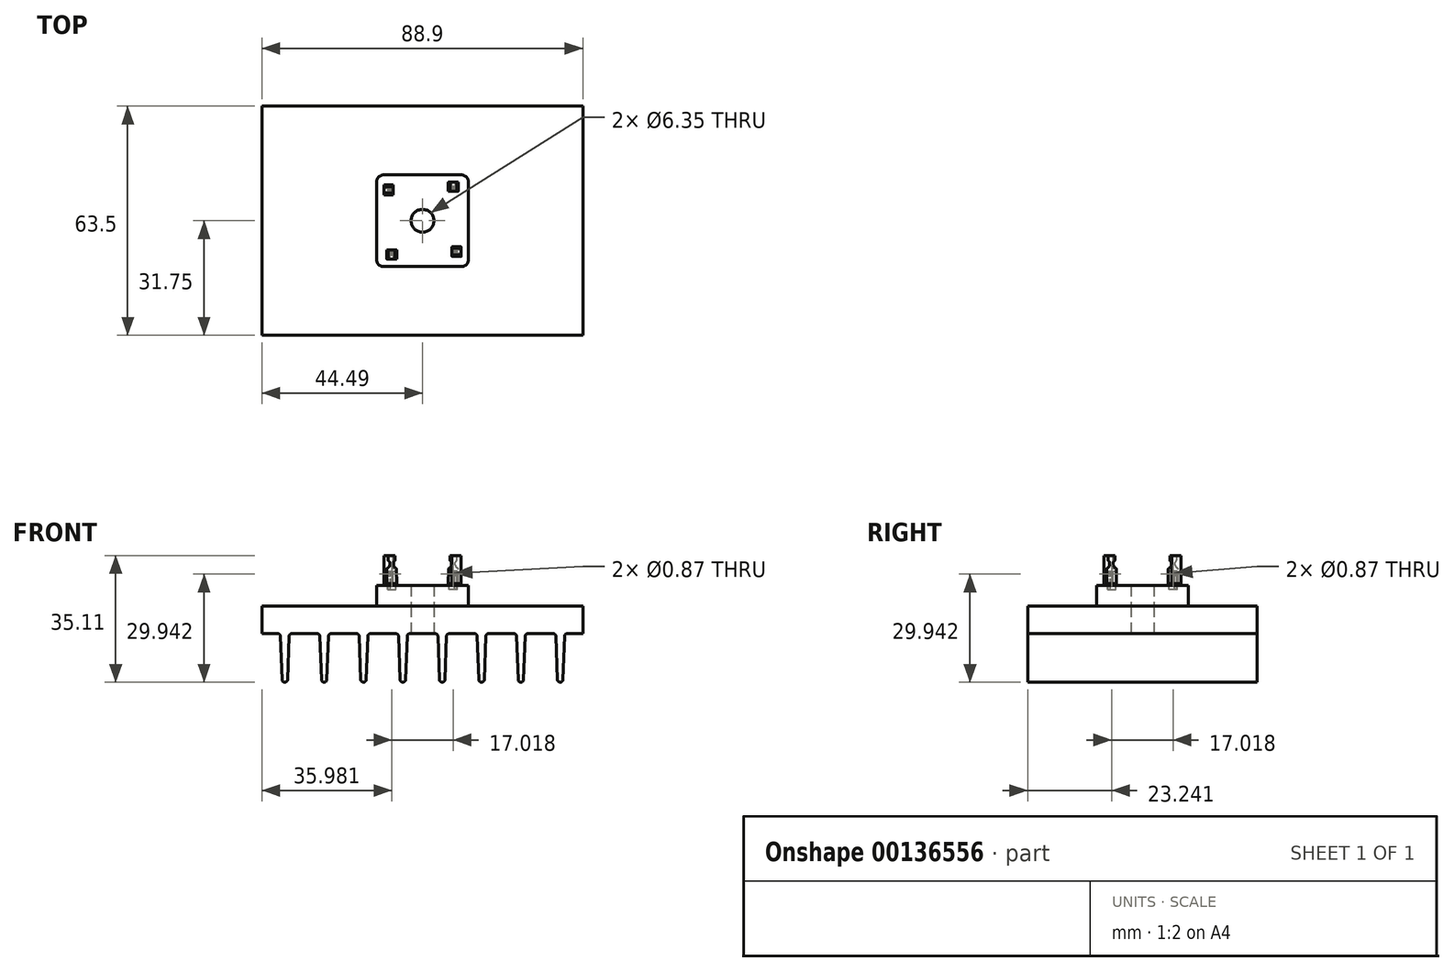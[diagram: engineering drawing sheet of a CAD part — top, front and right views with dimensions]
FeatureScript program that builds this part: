
annotation { "Feature Type Name" : "Feature", "Feature Type Description" : "" }
export const myFeature = defineFeature(function(context is Context, id is Id, definition is map)
    precondition{}
    {
        {
            var Q0;
            Q0=qCreatedBy(makeId("Front.planeOp"),FACE);
            var sketch = newSketch(context, id + "F0", { "sketchPlane" : qUnion([Q0])});
            skLineSegment(sketch, "E0.bottom", {"start": v(-44.49, 7.62) * mm, "end": v(44.41, 7.62) * mm});
            skLineSegment(sketch, "E0.top", {"start": v(-44.49, 0) * mm, "end": v(-40.1, 0) * mm});
            skLineSegment(sketch, "E0.left", {"start": v(-44.49, 7.62) * mm, "end": v(-44.49, 0) * mm});
            skLineSegment(sketch, "E0.right", {"start": v(44.41, 7.62) * mm, "end": v(44.41, 0) * mm});
            skPoint(sketch, "E1", {"position": v(0, 0) * mm});
            skArc(sketch, "E2", {"start": v(-38.9, -12.73) * mm, "mid": v(-38.14, -13.46) * mm, "end": v(-37.38, -12.73) * mm});
            skLineSegment(sketch, "E3", {"start": v(-37.38, -12.73) * mm, "end": v(-36.95, -0.73) * mm});
            skLineSegment(sketch, "E4", {"start": v(-36.92, 0) * mm, "end": v(-39.36, 0) * mm});
            skLineSegment(sketch, "E5", {"start": v(-39.33, -0.73) * mm, "end": v(-38.9, -12.73) * mm});
            skLineSegment(sketch, "E6", {"start": v(-38.14, -12.7) * mm, "end": v(-38.14, 0) * mm, "construction": true});
            skPoint(sketch, "E7.newPointB", {"position": v(44.49, 0) * mm});
            skArc(sketch, "E7.filletArc", {"start": v(-39.33, -0.73) * mm, "mid": v(-39.56, -0.21) * mm, "end": v(-40.1, 0) * mm});
            skLineSegment(sketch, "E8", {"start": v(44.41, 0) * mm, "end": v(40.1, 0) * mm});
            skPoint(sketch, "E9.visualSharp", {"position": v(-36.92, 0) * mm});
            skArc(sketch, "E9.filletArc", {"start": v(-36.18, 0) * mm, "mid": v(-36.71, -0.21) * mm, "end": v(-36.95, -0.73) * mm});
            skArc(sketch, "E10.1.0.0", {"start": v(-25.29, 0) * mm, "mid": v(-25.82, -0.21) * mm, "end": v(-26.05, -0.73) * mm});
            skLineSegment(sketch, "E10.1.0.1", {"start": v(-28.43, -0.73) * mm, "end": v(-28, -12.73) * mm});
            skArc(sketch, "E10.1.0.2", {"start": v(-28, -12.73) * mm, "mid": v(-27.24, -13.46) * mm, "end": v(-26.48, -12.73) * mm});
            skLineSegment(sketch, "E10.1.0.3", {"start": v(-26.48, -12.73) * mm, "end": v(-26.05, -0.73) * mm});
            skArc(sketch, "E10.1.0.4", {"start": v(-28.43, -0.73) * mm, "mid": v(-28.67, -0.21) * mm, "end": v(-29.2, 0) * mm});
            skArc(sketch, "E10.2.0.0", {"start": v(-14.4, 0) * mm, "mid": v(-14.92, -0.21) * mm, "end": v(-15.15, -0.73) * mm});
            skLineSegment(sketch, "E10.2.0.1", {"start": v(-17.54, -0.73) * mm, "end": v(-17.1, -12.73) * mm});
            skArc(sketch, "E10.2.0.2", {"start": v(-17.1, -12.73) * mm, "mid": v(-16.34, -13.46) * mm, "end": v(-15.58, -12.73) * mm});
            skLineSegment(sketch, "E10.2.0.3", {"start": v(-15.58, -12.73) * mm, "end": v(-15.15, -0.73) * mm});
            skArc(sketch, "E10.2.0.4", {"start": v(-17.54, -0.73) * mm, "mid": v(-17.77, -0.21) * mm, "end": v(-18.3, 0) * mm});
            skArc(sketch, "E10.3.0.0", {"start": v(-3.5, 0) * mm, "mid": v(-4.02, -0.21) * mm, "end": v(-4.26, -0.73) * mm});
            skLineSegment(sketch, "E10.3.0.1", {"start": v(-6.64, -0.73) * mm, "end": v(-6.2, -12.73) * mm});
            skArc(sketch, "E10.3.0.2", {"start": v(-6.2, -12.73) * mm, "mid": v(-5.45, -13.46) * mm, "end": v(-4.69, -12.73) * mm});
            skLineSegment(sketch, "E10.3.0.3", {"start": v(-4.69, -12.73) * mm, "end": v(-4.26, -0.73) * mm});
            skArc(sketch, "E10.3.0.4", {"start": v(-6.64, -0.73) * mm, "mid": v(-6.87, -0.21) * mm, "end": v(-7.4, 0) * mm});
            skArc(sketch, "E10.4.0.0", {"start": v(7.4, 0) * mm, "mid": v(6.87, -0.21) * mm, "end": v(6.64, -0.73) * mm});
            skLineSegment(sketch, "E10.4.0.1", {"start": v(4.26, -0.73) * mm, "end": v(4.69, -12.73) * mm});
            skArc(sketch, "E10.4.0.2", {"start": v(4.69, -12.73) * mm, "mid": v(5.45, -13.46) * mm, "end": v(6.2, -12.73) * mm});
            skLineSegment(sketch, "E10.4.0.3", {"start": v(6.2, -12.73) * mm, "end": v(6.64, -0.73) * mm});
            skArc(sketch, "E10.4.0.4", {"start": v(4.26, -0.73) * mm, "mid": v(4.02, -0.21) * mm, "end": v(3.5, 0) * mm});
            skArc(sketch, "E10.5.0.0", {"start": v(18.3, 0) * mm, "mid": v(17.77, -0.21) * mm, "end": v(17.54, -0.73) * mm});
            skLineSegment(sketch, "E10.5.0.1", {"start": v(15.15, -0.73) * mm, "end": v(15.58, -12.73) * mm});
            skArc(sketch, "E10.5.0.2", {"start": v(15.58, -12.73) * mm, "mid": v(16.34, -13.46) * mm, "end": v(17.1, -12.73) * mm});
            skLineSegment(sketch, "E10.5.0.3", {"start": v(17.1, -12.73) * mm, "end": v(17.54, -0.73) * mm});
            skArc(sketch, "E10.5.0.4", {"start": v(15.15, -0.73) * mm, "mid": v(14.92, -0.21) * mm, "end": v(14.4, 0) * mm});
            skArc(sketch, "E10.6.0.0", {"start": v(29.2, 0) * mm, "mid": v(28.67, -0.21) * mm, "end": v(28.43, -0.73) * mm});
            skLineSegment(sketch, "E10.6.0.1", {"start": v(26.05, -0.73) * mm, "end": v(26.48, -12.73) * mm});
            skArc(sketch, "E10.6.0.2", {"start": v(26.48, -12.73) * mm, "mid": v(27.24, -13.46) * mm, "end": v(28, -12.73) * mm});
            skLineSegment(sketch, "E10.6.0.3", {"start": v(28, -12.73) * mm, "end": v(28.43, -0.73) * mm});
            skArc(sketch, "E10.6.0.4", {"start": v(26.05, -0.73) * mm, "mid": v(25.82, -0.21) * mm, "end": v(25.29, 0) * mm});
            skArc(sketch, "E10.7.0.0", {"start": v(40.1, 0) * mm, "mid": v(39.56, -0.21) * mm, "end": v(39.33, -0.73) * mm});
            skLineSegment(sketch, "E10.7.0.1", {"start": v(36.95, -0.73) * mm, "end": v(37.38, -12.73) * mm});
            skArc(sketch, "E10.7.0.2", {"start": v(37.38, -12.73) * mm, "mid": v(38.14, -13.46) * mm, "end": v(38.9, -12.73) * mm});
            skLineSegment(sketch, "E10.7.0.3", {"start": v(38.9, -12.73) * mm, "end": v(39.33, -0.73) * mm});
            skArc(sketch, "E10.7.0.4", {"start": v(36.95, -0.73) * mm, "mid": v(36.71, -0.21) * mm, "end": v(36.18, 0) * mm});
            skLineSegment(sketch, "E10.direction1", {"start": v(-40.1, -0.76) * mm, "end": v(-29.2, -0.76) * mm, "construction": true});
            skLineSegment(sketch, "E11.trimOffspring", {"start": v(-29.2, 0) * mm, "end": v(-36.18, 0) * mm});
            skLineSegment(sketch, "E12.trimOffspring", {"start": v(-18.3, 0) * mm, "end": v(-25.29, 0) * mm});
            skLineSegment(sketch, "E13.trimOffspring", {"start": v(-7.4, 0) * mm, "end": v(-14.4, 0) * mm});
            skLineSegment(sketch, "E14.trimOffspring", {"start": v(3.5, 0) * mm, "end": v(-3.5, 0) * mm});
            skLineSegment(sketch, "E15.trimOffspring", {"start": v(14.4, 0) * mm, "end": v(7.4, 0) * mm});
            skLineSegment(sketch, "E16.trimOffspring", {"start": v(25.29, 0) * mm, "end": v(18.3, 0) * mm});
            skLineSegment(sketch, "E17.trimOffspring", {"start": v(36.18, 0) * mm, "end": v(29.2, 0) * mm});
            skSolve(sketch);
        }
        {
            var Q0;
            Q0 = qSketchRegion(id + "F0", true);
            extrude(context, id + "F1", {"entities" : qUnion([Q0]), "endBound" : BoundingType.SYMMETRIC, "depth" : 63.5 * mm});
        }
        {
            var Q0;
            Q0=makeQuery(id+"F1.opExtrude","SWEPT_FACE",FACE,{"disambiguationData":[OSD([sQuery(id+"F0.wireOp",EDGE,"E0.bottom")])]});
            var sketch = newSketch(context, id + "F2", { "sketchPlane" : qUnion([Q0])});
            skCircle(sketch, "E18", {"center": v(0, 0) * mm, "radius": 3.18 * mm});
            skSolve(sketch);
        }
        {
            var Q0;
            Q0 = qSketchRegion(id + "F2", true);
            extrude(context, id + "F3", {"entities" : qUnion([Q0]), "endBound" : BoundingType.SYMMETRIC, "depth" : 76.2 * mm});
        }
        {
            var Q0;
            Q0=makeQuery(id+"F3.opExtrude","SWEPT_BODY",BODY,{"disambiguationData":[OSD([sQuery(id+"F2.wireOp",EDGE,"E18")])]});
            var Q1;
            Q1=makeQuery(id+"F1.opExtrude","SWEPT_BODY",BODY,{"disambiguationData":[OSD([sQuery(id+"F0.wireOp",EDGE,"E0.bottom"),sQuery(id+"F0.wireOp",EDGE,"E0.top"),sQuery(id+"F0.wireOp",EDGE,"E0.left"),sQuery(id+"F0.wireOp",EDGE,"E0.right"),sQuery(id+"F0.wireOp",EDGE,"E2"),sQuery(id+"F0.wireOp",EDGE,"E3"),sQuery(id+"F0.wireOp",EDGE,"E5"),sQuery(id+"F0.wireOp",EDGE,"E7.filletArc"),sQuery(id+"F0.wireOp",EDGE,"E8"),sQuery(id+"F0.wireOp",EDGE,"E9.filletArc"),sQuery(id+"F0.wireOp",EDGE,"E10.1.0.0"),sQuery(id+"F0.wireOp",EDGE,"E10.1.0.1"),sQuery(id+"F0.wireOp",EDGE,"E10.1.0.2"),sQuery(id+"F0.wireOp",EDGE,"E10.1.0.3"),sQuery(id+"F0.wireOp",EDGE,"E10.1.0.4"),sQuery(id+"F0.wireOp",EDGE,"E10.2.0.0"),sQuery(id+"F0.wireOp",EDGE,"E10.2.0.1"),sQuery(id+"F0.wireOp",EDGE,"E10.2.0.2"),sQuery(id+"F0.wireOp",EDGE,"E10.2.0.3"),sQuery(id+"F0.wireOp",EDGE,"E10.2.0.4"),sQuery(id+"F0.wireOp",EDGE,"E10.3.0.0"),sQuery(id+"F0.wireOp",EDGE,"E10.3.0.1"),sQuery(id+"F0.wireOp",EDGE,"E10.3.0.2"),sQuery(id+"F0.wireOp",EDGE,"E10.3.0.3"),sQuery(id+"F0.wireOp",EDGE,"E10.3.0.4"),sQuery(id+"F0.wireOp",EDGE,"E10.4.0.0"),sQuery(id+"F0.wireOp",EDGE,"E10.4.0.1"),sQuery(id+"F0.wireOp",EDGE,"E10.4.0.2"),sQuery(id+"F0.wireOp",EDGE,"E10.4.0.3"),sQuery(id+"F0.wireOp",EDGE,"E10.4.0.4"),sQuery(id+"F0.wireOp",EDGE,"E10.5.0.0"),sQuery(id+"F0.wireOp",EDGE,"E10.5.0.1"),sQuery(id+"F0.wireOp",EDGE,"E10.5.0.2"),sQuery(id+"F0.wireOp",EDGE,"E10.5.0.3"),sQuery(id+"F0.wireOp",EDGE,"E10.5.0.4"),sQuery(id+"F0.wireOp",EDGE,"E10.6.0.0"),sQuery(id+"F0.wireOp",EDGE,"E10.6.0.1"),sQuery(id+"F0.wireOp",EDGE,"E10.6.0.2"),sQuery(id+"F0.wireOp",EDGE,"E10.6.0.3"),sQuery(id+"F0.wireOp",EDGE,"E10.6.0.4"),sQuery(id+"F0.wireOp",EDGE,"E10.7.0.0"),sQuery(id+"F0.wireOp",EDGE,"E10.7.0.1"),sQuery(id+"F0.wireOp",EDGE,"E10.7.0.2"),sQuery(id+"F0.wireOp",EDGE,"E10.7.0.3"),sQuery(id+"F0.wireOp",EDGE,"E10.7.0.4"),sQuery(id+"F0.wireOp",EDGE,"E11.trimOffspring"),sQuery(id+"F0.wireOp",EDGE,"E12.trimOffspring"),sQuery(id+"F0.wireOp",EDGE,"E13.trimOffspring"),sQuery(id+"F0.wireOp",EDGE,"E14.trimOffspring"),sQuery(id+"F0.wireOp",EDGE,"E15.trimOffspring"),sQuery(id+"F0.wireOp",EDGE,"E16.trimOffspring"),sQuery(id+"F0.wireOp",EDGE,"E17.trimOffspring")])]});
            booleanBodies(context, id + "F4", {"operationType" : BooleanOperationType.SUBTRACTION, "tools" : qUnion([Q0]), "targets" : qUnion([Q1])});
        }
        {
            var Q0;
            Q0=makeQuery(id+"F1.opExtrude","SWEPT_FACE",FACE,{"disambiguationData":[OSD([sQuery(id+"F0.wireOp",EDGE,"E0.bottom")])]});
            var sketch = newSketch(context, id + "F5", { "sketchPlane" : qUnion([Q0])});
            skLineSegment(sketch, "E19.bottom", {"start": v(12.7, -12.7) * mm, "end": v(-12.7, -12.7) * mm});
            skLineSegment(sketch, "E19.top", {"start": v(12.7, 12.7) * mm, "end": v(-12.7, 12.7) * mm});
            skLineSegment(sketch, "E19.left", {"start": v(12.7, -12.7) * mm, "end": v(12.7, 12.7) * mm});
            skLineSegment(sketch, "E19.right", {"start": v(-12.7, -12.7) * mm, "end": v(-12.7, 12.7) * mm});
            skPoint(sketch, "E19.middle", {"position": v(0, 0) * mm});
            skCircle(sketch, "E20.0", {"center": v(0, 0) * mm, "radius": 3.18 * mm});
            skSolve(sketch);
        }
        {
            var Q0;
            Q0 = qSketchRegion(id + "F5", true);
            extrude(context, id + "F6", {"entities" : qUnion([Q0]), "depth" : 5.7 * mm});
        }
        {
            var Q0;
            Q0=makeQuery(id+"F6.opExtrude","SWEPT_FACE",FACE,{"disambiguationData":[OSD([sQuery(id+"F5.wireOp",EDGE,"E19.bottom")])]});
            cPlane(context, id + "F7", {"entities" : qUnion([Q0]), "cplaneType" : CPlaneType.OFFSET, "offset" : 3.8 * mm, "oppositeDirection" : true, "width" : 152.4 * mm, "height" : 152.4 * mm});
        }
        {
            var Q0;
            Q0=qCreatedBy(id+"F7.planeOp",FACE);
            var sketch = newSketch(context, id + "F8", { "sketchPlane" : qUnion([Q0])});
            skLineSegment(sketch, "E21.bottom", {"start": v(-9.65, 12.25) * mm, "end": v(-7.37, 12.25) * mm});
            skLineSegment(sketch, "E21.top", {"start": v(-9.65, 17.3) * mm, "end": v(-7.37, 17.3) * mm});
            skLineSegment(sketch, "E21.left", {"start": v(-9.65, 12.25) * mm, "end": v(-9.65, 17.3) * mm});
            skLineSegment(sketch, "E21.right", {"start": v(-7.37, 12.25) * mm, "end": v(-7.37, 17.3) * mm});
            skCircle(sketch, "E22", {"center": v(-8.5, 16.48) * mm, "radius": 0.43 * mm});
            skPoint(sketch, "E22.centerSnap0", {"position": v(-8.5, 17.3) * mm});
            skSolve(sketch);
        }
        {
            var Q0;
            Q0 = qSketchRegion(id + "F8", true);
            extrude(context, id + "F9", {"entities" : qUnion([Q0]), "depth" : 0.6 * mm});
        }
        {
            var Q0;
            Q0=makeQuery(id+"F6.opExtrude","SWEPT_EDGE",EDGE,{"disambiguationData":[OSD([sQuery(id+"F5.wireOp",EDGE,"E19.bottom"),sQuery(id+"F5.wireOp",EDGE,"E19.left")])]});
            var Q1;
            Q1=makeQuery(id+"F6.opExtrude","SWEPT_EDGE",EDGE,{"disambiguationData":[OSD([sQuery(id+"F5.wireOp",EDGE,"E19.bottom"),sQuery(id+"F5.wireOp",EDGE,"E19.right")])]});
            var Q2;
            Q2=makeQuery(id+"F6.opExtrude","SWEPT_EDGE",EDGE,{"disambiguationData":[OSD([sQuery(id+"F5.wireOp",EDGE,"E19.top"),sQuery(id+"F5.wireOp",EDGE,"E19.left")])]});
            var Q3;
            Q3=makeQuery(id+"F6.opExtrude","SWEPT_EDGE",EDGE,{"disambiguationData":[OSD([sQuery(id+"F5.wireOp",EDGE,"E19.top"),sQuery(id+"F5.wireOp",EDGE,"E19.right")])]});
            fillet(context, id + "F10", {"entities" : qUnion([Q0, Q1, Q2, Q3]), "radius" : 1.9 * mm, "tangentPropagation" : true, "allowEdgeOverflow" : false});
        }
        {
            var Q0;
            Q0=qCreatedBy(makeId("Front.planeOp"),FACE);
            var sketch = newSketch(context, id + "F11", { "sketchPlane" : qUnion([Q0])});
            skLineSegment(sketch, "E23", {"start": v(0, 68.14) * mm, "end": v(0, -52.26) * mm});
            skSolve(sketch);
        }
        {
            var Q0;
            Q0=makeQuery(id+"F9.opExtrude","SWEPT_BODY",BODY,{"disambiguationData":[OSD([sQuery(id+"F8.wireOp",EDGE,"E21.bottom"),sQuery(id+"F8.wireOp",EDGE,"E21.top"),sQuery(id+"F8.wireOp",EDGE,"E21.left"),sQuery(id+"F8.wireOp",EDGE,"E21.right"),sQuery(id+"F8.wireOp",EDGE,"E22")])]});
            var Q1;
            Q1=sQuery(id+"F11.wireOp",EDGE,"E23");
            circularPattern(context, id + "F12", {"entities" : qUnion([Q0]), "axis" : qUnion([Q1]), "angle" : 90 * degree, "instanceCount" : 4});
        }
        {
            var Q0;
            Q0=qCreatedBy(id+"F7.planeOp",FACE);
            var sketch = newSketch(context, id + "F13", { "sketchPlane" : qUnion([Q0])});
            skLineSegment(sketch, "E24", {"start": v(-9.9, 13.87) * mm, "end": v(-9.9, 17.84) * mm});
            skLineSegment(sketch, "E25", {"start": v(-9.9, 13.87) * mm, "end": v(-8.53, 13.87) * mm});
            skLineSegment(sketch, "E26", {"start": v(-9.06, 19.13) * mm, "end": v(-9.06, 19.68) * mm});
            skLineSegment(sketch, "E27", {"start": v(-9.5, 20.42) * mm, "end": v(-9.5, 21.64) * mm});
            skArc(sketch, "E28", {"start": v(-9.68, 18.18) * mm, "mid": v(-9.84, 18.04) * mm, "end": v(-9.9, 17.84) * mm});
            skArc(sketch, "E29", {"start": v(-9.68, 18.18) * mm, "mid": v(-9.23, 18.56) * mm, "end": v(-9.06, 19.13) * mm});
            skArc(sketch, "E30", {"start": v(-9.06, 19.68) * mm, "mid": v(-9.12, 19.88) * mm, "end": v(-9.27, 20.02) * mm});
            skArc(sketch, "E31", {"start": v(-9.5, 20.42) * mm, "mid": v(-9.44, 20.2) * mm, "end": v(-9.27, 20.02) * mm});
            skLineSegment(sketch, "E32", {"start": v(-9.5, 21.64) * mm, "end": v(-8.56, 21.64) * mm});
            skLineSegment(sketch, "E33", {"start": v(-8.56, 21.64) * mm, "end": v(-8.53, 13.87) * mm, "construction": true});
            skLineSegment(sketch, "E34.MirrorCS", {"start": v(-7.16, 13.88) * mm, "end": v(-8.53, 13.87) * mm});
            skLineSegment(sketch, "E35.MirrorCS", {"start": v(-8.05, 19.13) * mm, "end": v(-8.05, 19.68) * mm});
            skLineSegment(sketch, "E36.MirrorCS", {"start": v(-7.61, 20.43) * mm, "end": v(-7.63, 21.65) * mm});
            skLineSegment(sketch, "E37.MirrorCS", {"start": v(-7.63, 21.65) * mm, "end": v(-8.56, 21.64) * mm});
            skLineSegment(sketch, "E38.MirrorCS", {"start": v(-7.16, 13.88) * mm, "end": v(-7.2, 17.85) * mm});
            skArc(sketch, "E39", {"start": v(-7.85, 20.02) * mm, "mid": v(-7.68, 20.2) * mm, "end": v(-7.61, 20.43) * mm});
            skArc(sketch, "E40", {"start": v(-7.85, 20.02) * mm, "mid": v(-8, 19.88) * mm, "end": v(-8.05, 19.68) * mm});
            skArc(sketch, "E41", {"start": v(-7.2, 17.85) * mm, "mid": v(-7.25, 18.05) * mm, "end": v(-7.41, 18.18) * mm});
            skArc(sketch, "E42", {"start": v(-8.05, 19.13) * mm, "mid": v(-7.87, 18.56) * mm, "end": v(-7.41, 18.18) * mm});
            skSolve(sketch);
        }
        {
            var Q0;
            Q0 = qSketchRegion(id + "F13", true);
            extrude(context, id + "F14", {"entities" : qUnion([Q0]), "depth" : 1.78 * mm, "hasSecondDirection" : true, "secondDirectionOppositeDirection" : true, "secondDirectionDepth" : 0.76 * mm});
        }
        {
            var Q0;
            Q0=makeQuery(id+"F14.opExtrude","SWEPT_BODY",BODY,{"disambiguationData":[OSD([sQuery(id+"F13.wireOp",EDGE,"E24"),sQuery(id+"F13.wireOp",EDGE,"E25"),sQuery(id+"F13.wireOp",EDGE,"E26"),sQuery(id+"F13.wireOp",EDGE,"E27"),sQuery(id+"F13.wireOp",EDGE,"E28"),sQuery(id+"F13.wireOp",EDGE,"E29"),sQuery(id+"F13.wireOp",EDGE,"E30"),sQuery(id+"F13.wireOp",EDGE,"E31"),sQuery(id+"F13.wireOp",EDGE,"E32"),sQuery(id+"F13.wireOp",EDGE,"E34.MirrorCS"),sQuery(id+"F13.wireOp",EDGE,"E35.MirrorCS"),sQuery(id+"F13.wireOp",EDGE,"E36.MirrorCS"),sQuery(id+"F13.wireOp",EDGE,"E37.MirrorCS"),sQuery(id+"F13.wireOp",EDGE,"E38.MirrorCS"),sQuery(id+"F13.wireOp",EDGE,"E39"),sQuery(id+"F13.wireOp",EDGE,"E40"),sQuery(id+"F13.wireOp",EDGE,"E41"),sQuery(id+"F13.wireOp",EDGE,"E42")])]});
            var Q1;
            Q1=sQuery(id+"F11.wireOp",EDGE,"E23");
            circularPattern(context, id + "F15", {"entities" : qUnion([Q0]), "axis" : qUnion([Q1]), "angle" : 90 * degree, "instanceCount" : 4});
        }
    });
